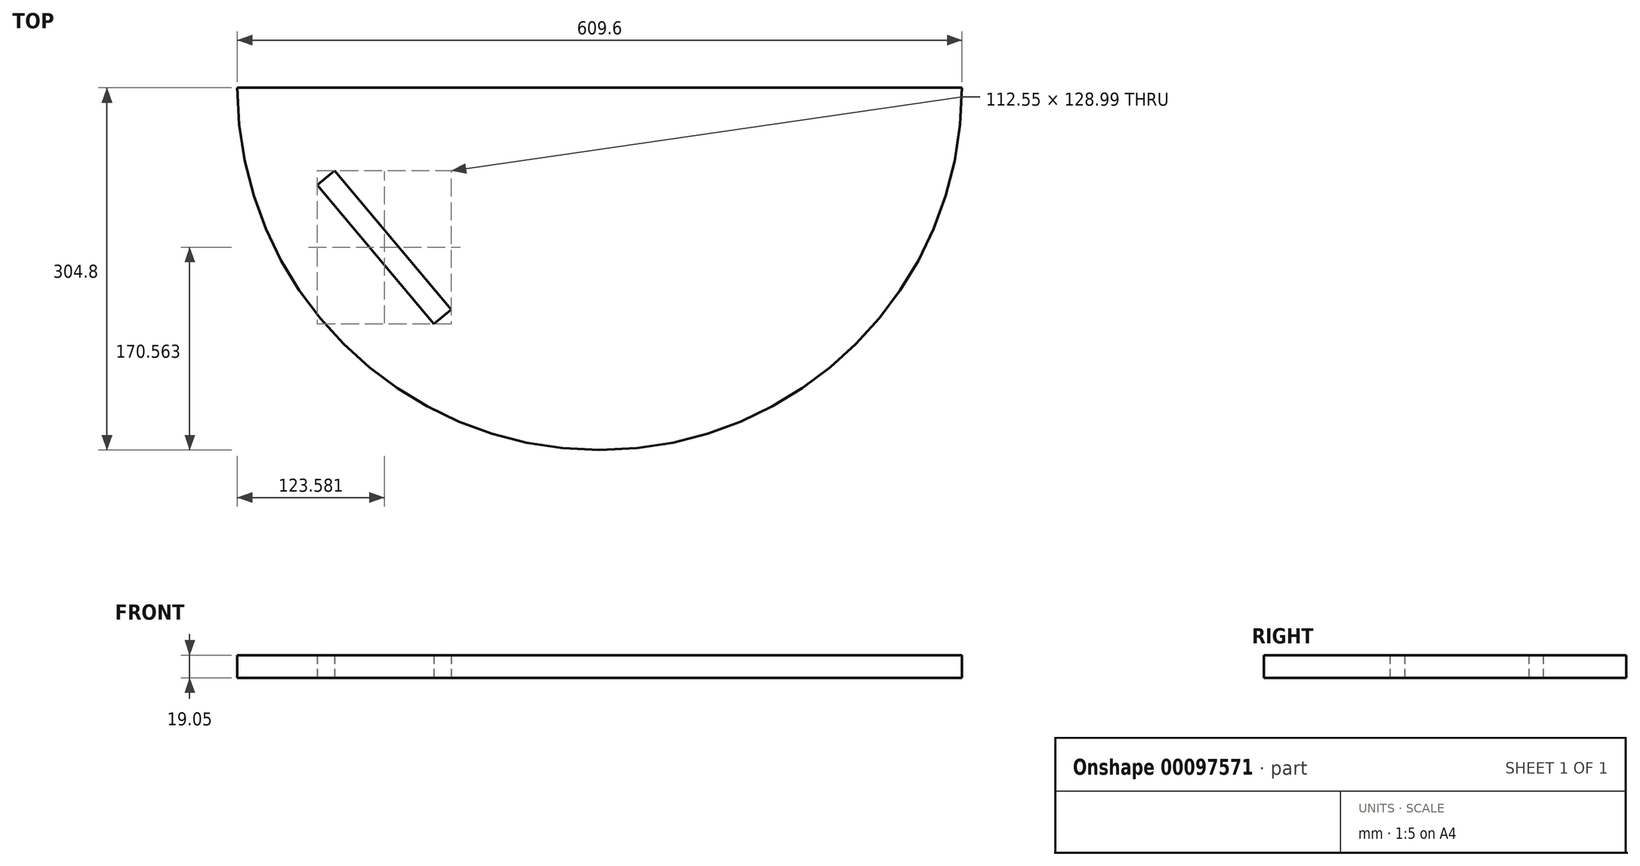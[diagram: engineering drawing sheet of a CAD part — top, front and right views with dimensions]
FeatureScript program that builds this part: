
annotation { "Feature Type Name" : "Feature", "Feature Type Description" : "" }
export const myFeature = defineFeature(function(context is Context, id is Id, definition is map)
    precondition{}
    {
        {
            var Q0;
            Q0=qCreatedBy(makeId("Top.planeOp"),FACE);
            var sketch = newSketch(context, id + "F0", { "sketchPlane" : qUnion([Q0])});
            skArc(sketch, "E0", {"start": v(-304.8, 0) * mm, "mid": v(0, -304.8) * mm, "end": v(304.8, 0) * mm});
            skLineSegment(sketch, "E1", {"start": v(241.3, 0) * mm, "end": v(304.8, 0) * mm});
            skLineSegment(sketch, "E2", {"start": v(-249.2, 0) * mm, "end": v(-304.8, 0) * mm});
            skArc(sketch, "E3", {"start": v(-93.42, -222.48) * mm, "mid": v(133.57, -200.96) * mm, "end": v(241.3, 0) * mm});
            skLineSegment(sketch, "E4", {"start": v(-249.2, 0) * mm, "end": v(241.3, 0) * mm});
            skLineSegment(sketch, "E5.bottom", {"start": v(-237.5, -81.99) * mm, "end": v(-222.9, -69.74) * mm});
            skLineSegment(sketch, "E5.top", {"start": v(-139.54, -198.73) * mm, "end": v(-124.94, -186.49) * mm});
            skLineSegment(sketch, "E5.left", {"start": v(-237.5, -81.99) * mm, "end": v(-139.54, -198.73) * mm});
            skLineSegment(sketch, "E5.right", {"start": v(-222.9, -69.74) * mm, "end": v(-124.94, -186.49) * mm});
            skSolve(sketch);
        }
        {
            var Q0;
            Q0 = qSketchRegion(id + "F0", true);
            extrude(context, id + "F1", {"entities" : qUnion([Q0]), "depth" : 19.05 * mm, "offsetDistance" : 25.4 * mm});
        }
    });
